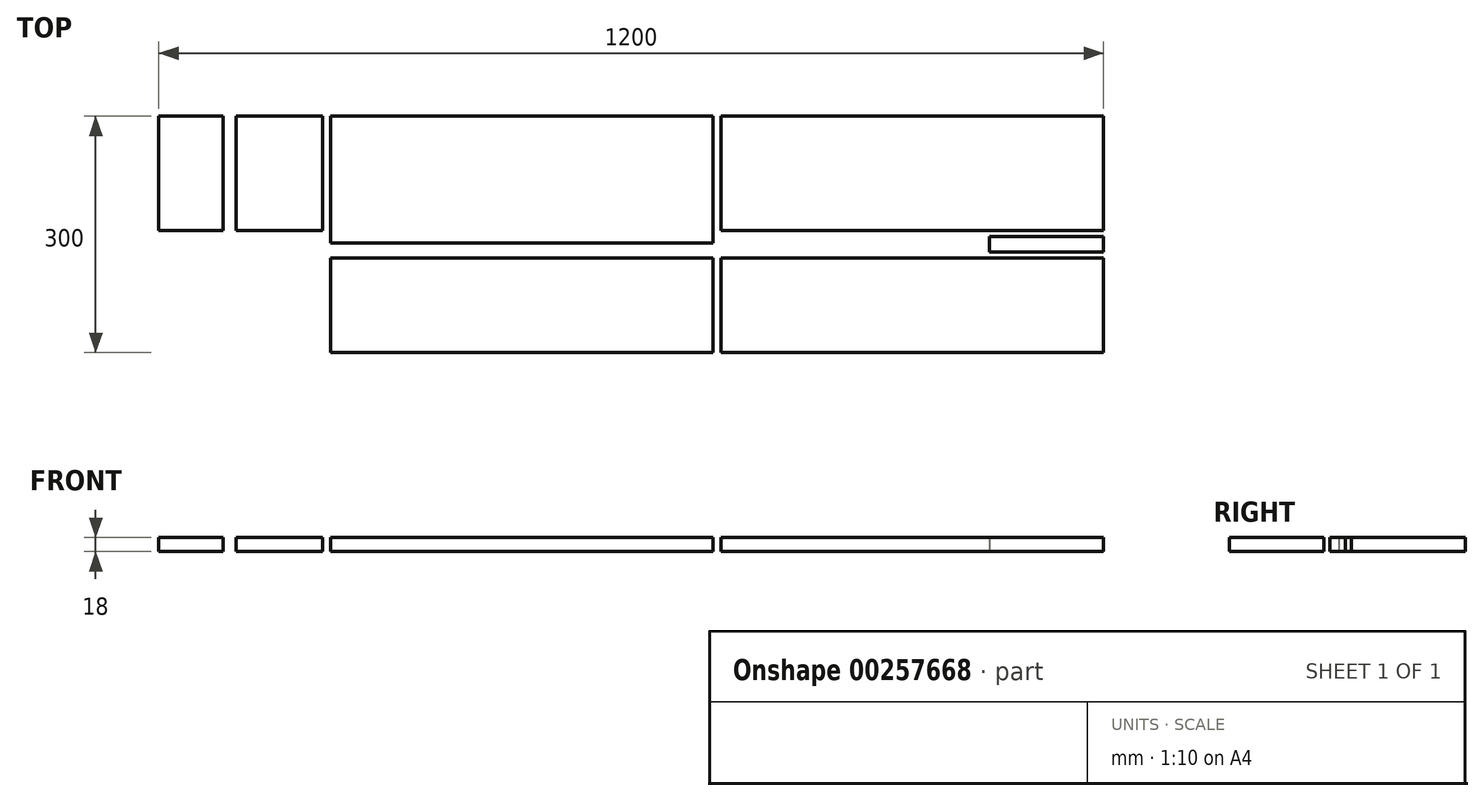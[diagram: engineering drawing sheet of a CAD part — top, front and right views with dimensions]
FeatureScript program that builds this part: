
annotation { "Feature Type Name" : "Feature", "Feature Type Description" : "" }
export const myFeature = defineFeature(function(context is Context, id is Id, definition is map)
    precondition{}
    {
        {
            var Q0;
            Q0=qCreatedBy(makeId("Top.planeOp"),FACE);
            var sketch = newSketch(context, id + "F0", { "sketchPlane" : qUnion([Q0])});
            skLineSegment(sketch, "E0.bottom", {"start": v(600, 150) * mm, "end": v(-600, 150) * mm, "construction": true});
            skLineSegment(sketch, "E0.top", {"start": v(600, -150) * mm, "end": v(-600, -150) * mm, "construction": true});
            skLineSegment(sketch, "E0.left", {"start": v(600, 150) * mm, "end": v(600, -150) * mm, "construction": true});
            skLineSegment(sketch, "E0.right", {"start": v(-600, 150) * mm, "end": v(-600, -150) * mm, "construction": true});
            skPoint(sketch, "E0.middle", {"position": v(0, 0) * mm});
            skLineSegment(sketch, "E1.bottom", {"start": v(600, 150) * mm, "end": v(114, 150) * mm});
            skLineSegment(sketch, "E1.top", {"start": v(600, 5) * mm, "end": v(114, 5) * mm});
            skLineSegment(sketch, "E1.left", {"start": v(600, 150) * mm, "end": v(600, 5) * mm});
            skLineSegment(sketch, "E1.right", {"start": v(114, 150) * mm, "end": v(114, 5) * mm});
            skLineSegment(sketch, "E2.bottom", {"start": v(104, 150) * mm, "end": v(-382, 150) * mm});
            skLineSegment(sketch, "E2.top", {"start": v(104, -11) * mm, "end": v(-382, -11) * mm});
            skLineSegment(sketch, "E2.left", {"start": v(104, 150) * mm, "end": v(104, -11) * mm});
            skLineSegment(sketch, "E2.right", {"start": v(-382, 150) * mm, "end": v(-382, -11) * mm});
            skLineSegment(sketch, "E3.bottom", {"start": v(600, -150) * mm, "end": v(114, -150) * mm});
            skLineSegment(sketch, "E3.top", {"start": v(600, -30) * mm, "end": v(114, -30) * mm});
            skLineSegment(sketch, "E3.left", {"start": v(600, -150) * mm, "end": v(600, -30) * mm});
            skLineSegment(sketch, "E3.right", {"start": v(114, -150) * mm, "end": v(114, -30) * mm});
            skLineSegment(sketch, "E4.bottom", {"start": v(104, -30) * mm, "end": v(-382, -30) * mm});
            skLineSegment(sketch, "E4.top", {"start": v(104, -150) * mm, "end": v(-382, -150) * mm});
            skLineSegment(sketch, "E4.left", {"start": v(104, -30) * mm, "end": v(104, -150) * mm});
            skLineSegment(sketch, "E4.right", {"start": v(-382, -30) * mm, "end": v(-382, -150) * mm});
            skLineSegment(sketch, "E5.bottom", {"start": v(-392, 150) * mm, "end": v(-502, 150) * mm});
            skLineSegment(sketch, "E5.top", {"start": v(-392, 5) * mm, "end": v(-502, 5) * mm});
            skLineSegment(sketch, "E5.left", {"start": v(-392, 150) * mm, "end": v(-392, 5) * mm});
            skLineSegment(sketch, "E5.right", {"start": v(-502, 150) * mm, "end": v(-502, 5) * mm});
            skLineSegment(sketch, "E6.bottom", {"start": v(-600, 150) * mm, "end": v(-518, 150) * mm});
            skLineSegment(sketch, "E6.top", {"start": v(-600, 5) * mm, "end": v(-518, 5) * mm});
            skLineSegment(sketch, "E6.left", {"start": v(-600, 150) * mm, "end": v(-600, 5) * mm});
            skLineSegment(sketch, "E6.right", {"start": v(-518, 150) * mm, "end": v(-518, 5) * mm});
            skLineSegment(sketch, "E7.bottom", {"start": v(600, -2.5) * mm, "end": v(455, -2.5) * mm});
            skLineSegment(sketch, "E7.top", {"start": v(600, -22.5) * mm, "end": v(455, -22.5) * mm});
            skLineSegment(sketch, "E7.left", {"start": v(600, -2.5) * mm, "end": v(600, -22.5) * mm});
            skLineSegment(sketch, "E7.right", {"start": v(455, -2.5) * mm, "end": v(455, -22.5) * mm});
            skSolve(sketch);
        }
        {
            var Q0;
            Q0 = qSketchRegion(id + "F0", true);
            extrude(context, id + "F1", {"entities" : qUnion([Q0]), "depth" : 18 * mm});
        }
    });
